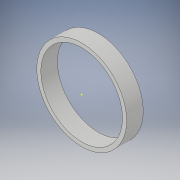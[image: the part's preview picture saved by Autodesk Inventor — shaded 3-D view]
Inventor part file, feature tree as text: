
AUTODESK INVENTOR PART (.ipt)
format: ipt  version: 2019 (Build 230136000, 136)  size: 105,984 bytes
history: native  units: mm
features: sketch x3, extrude x2
ambient origin geometry x8: Origin, YZ Plane, XZ Plane, XY Plane, X Axis, Y Axis, Z Axis, Center Point
bodies: Solid1 (feature_tree)
feature tree (5):
  extrude  "Extrusion1"  Depth=1.74mm TaperAngle=0.0deg
  sketch  "Sketch2"  dims[d3=8.56mm d4=1.74mm d5=0.0mm]
  extrude  "Extrusion2"  Depth=1.74mm TaperAngle=0.0deg
  sketch  "Sketch1"  dims[d0=9.42mm d1=1.74mm d2=0.0mm]
  sketch  "Sketch3"
